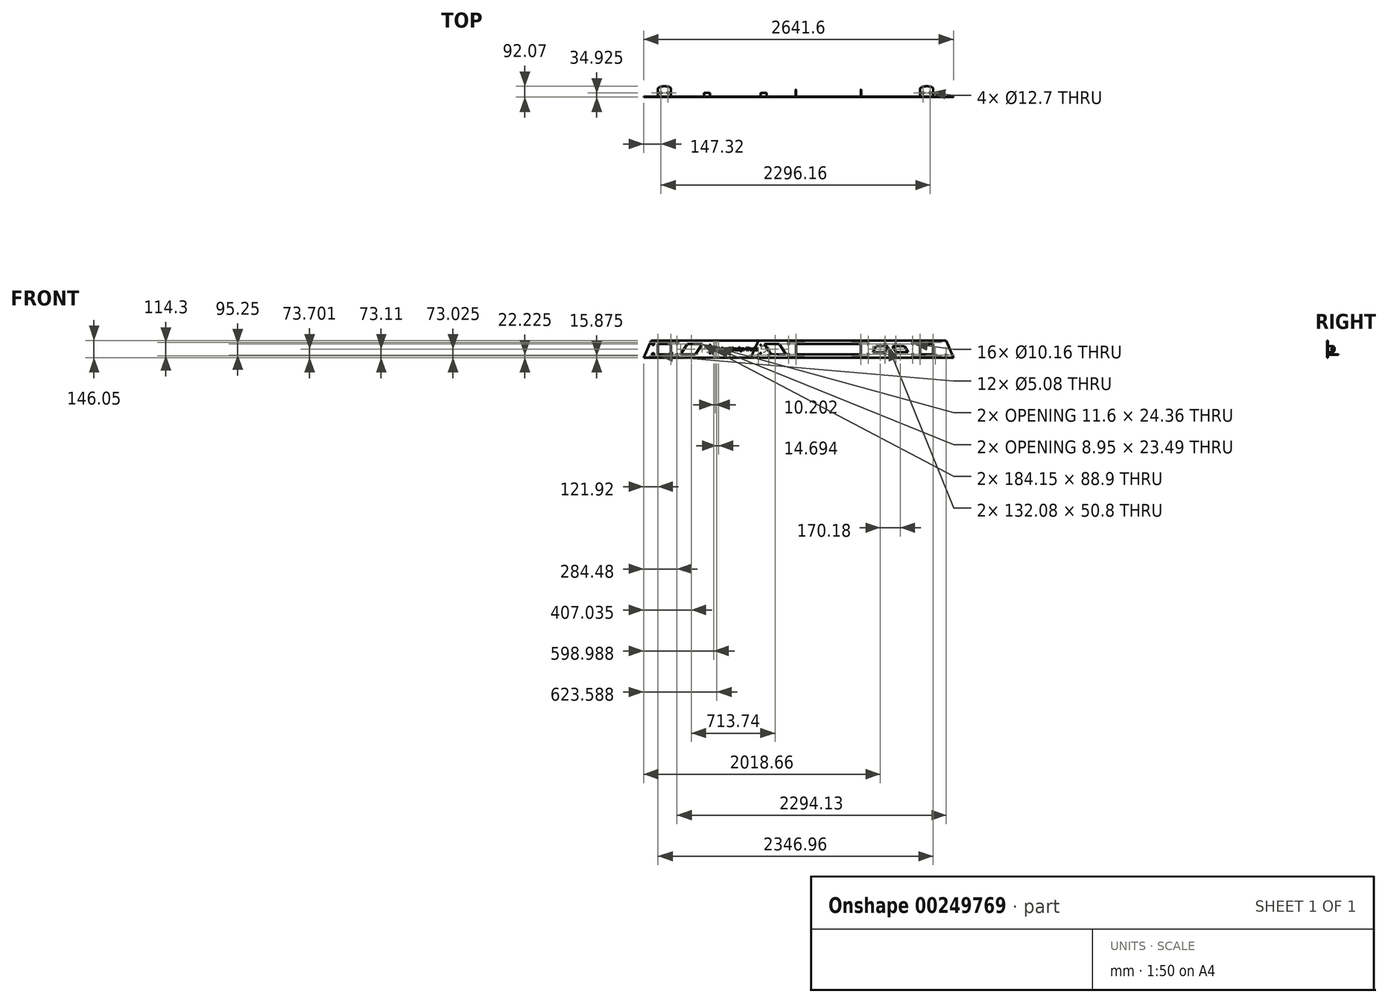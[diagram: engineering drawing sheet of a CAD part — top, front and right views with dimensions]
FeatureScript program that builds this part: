
annotation { "Feature Type Name" : "Feature", "Feature Type Description" : "" }
export const myFeature = defineFeature(function(context is Context, id is Id, definition is map)
    precondition{}
    {
        {
            var Q0;
            Q0=qCreatedBy(makeId("Front.planeOp"),FACE);
            var sketch = newSketch(context, id + "F0", { "sketchPlane" : qUnion([Q0])});
            skLineSegment(sketch, "E0", {"start": v(0, 0) * mm, "end": v(-863.6, 0) * mm});
            skLineSegment(sketch, "E1", {"start": v(-863.6, 0) * mm, "end": v(-800.1, 146.05) * mm});
            skLineSegment(sketch, "E2", {"start": v(-800.1, 146.05) * mm, "end": v(59.06, 146.05) * mm});
            skLineSegment(sketch, "E3", {"start": v(0, 0) * mm, "end": v(0, 425.14) * mm, "construction": true});
            skLineSegment(sketch, "E4.MirrorCS", {"start": v(800.1, 146.05) * mm, "end": v(-59.06, 146.05) * mm});
            skLineSegment(sketch, "E5.MirrorCS", {"start": v(863.6, 0) * mm, "end": v(800.1, 146.05) * mm});
            skLineSegment(sketch, "E6.MirrorCS", {"start": v(0, 0) * mm, "end": v(863.6, 0) * mm});
            skSolve(sketch);
        }
        {
            var Q0;
            Q0 = qSketchRegion(id + "F0", true);
            extrude(context, id + "F1", {"entities" : qUnion([Q0]), "oppositeDirection" : true, "depth" : 3.17 * mm});
        }
        {
            var Q0;
            Q0=makeQuery(id+"F1.opExtrude","CAP_FACE",FACE,{"disambiguationData":[OSD([sQuery(id+"F0.wireOp",EDGE,"E0"),sQuery(id+"F0.wireOp",EDGE,"E1"),sQuery(id+"F0.wireOp",EDGE,"E2"),sQuery(id+"F0.wireOp",EDGE,"E4.MirrorCS"),sQuery(id+"F0.wireOp",EDGE,"E5.MirrorCS"),sQuery(id+"F0.wireOp",EDGE,"E6.MirrorCS")])],"isStart":true});
            var sketch = newSketch(context, id + "F2", { "sketchPlane" : qUnion([Q0])});
            skLineSegment(sketch, "E7.0", {"start": v(-863.6, 0) * mm, "end": v(-800.1, 146.05) * mm});
            skLineSegment(sketch, "E8", {"start": v(-800.1, 146.05) * mm, "end": v(-1714.5, 146.05) * mm});
            skLineSegment(sketch, "E9", {"start": v(-1714.5, 146.05) * mm, "end": v(-1778, 0) * mm});
            skLineSegment(sketch, "E10", {"start": v(-1778, 0) * mm, "end": v(-863.6, 0) * mm});
            skSolve(sketch);
        }
        {
            var Q0;
            Q0 = qSketchRegion(id + "F2", true);
            var Q1;
            Q1=makeQuery(id+"F1.opExtrude","CAP_FACE",FACE,{"disambiguationData":[OSD([sQuery(id+"F0.wireOp",EDGE,"E0"),sQuery(id+"F0.wireOp",EDGE,"E1"),sQuery(id+"F0.wireOp",EDGE,"E2"),sQuery(id+"F0.wireOp",EDGE,"E4.MirrorCS"),sQuery(id+"F0.wireOp",EDGE,"E5.MirrorCS"),sQuery(id+"F0.wireOp",EDGE,"E6.MirrorCS")])],"isStart":false});
            extrude(context, id + "F3", {"entities" : qUnion([Q0]), "endBound" : BoundingType.UP_TO_SURFACE, "oppositeDirection" : true, "endBoundEntityFace" : qUnion([Q1]), "depth" : 25.4 * mm});
        }
        {
            var Q0;
            Q0=makeQuery(id+"F1.opExtrude","CAP_FACE",FACE,{"disambiguationData":[OSD([sQuery(id+"F0.wireOp",EDGE,"E0"),sQuery(id+"F0.wireOp",EDGE,"E1"),sQuery(id+"F0.wireOp",EDGE,"E2"),sQuery(id+"F0.wireOp",EDGE,"E4.MirrorCS"),sQuery(id+"F0.wireOp",EDGE,"E5.MirrorCS"),sQuery(id+"F0.wireOp",EDGE,"E6.MirrorCS")])],"isStart":false});
            var sketch = newSketch(context, id + "F4", { "sketchPlane" : qUnion([Q0])});
            skLineSegment(sketch, "E11", {"start": v(-831.85, 73.02) * mm, "end": v(1871.27, 73.02) * mm, "construction": true});
            skCircle(sketch, "E12", {"center": v(1236.69, 73.02) * mm, "radius": 25.4 * mm});
            skCircle(sketch, "E13", {"center": v(754.09, 73.02) * mm, "radius": 25.4 * mm});
            skSolve(sketch);
        }
        {
            var Q0;
            Q0 = qSketchRegion(id + "F4", true);
            extrude(context, id + "F5", {"entities" : qUnion([Q0]), "operationType" : NewBodyOperationType.ADD, "depth" : 31.75 * mm});
        }
        {
            var Q0;
            Q0=makeQuery(id+"F1.opExtrude","CAP_FACE",FACE,{"disambiguationData":[OSD([sQuery(id+"F0.wireOp",EDGE,"E0"),sQuery(id+"F0.wireOp",EDGE,"E1"),sQuery(id+"F0.wireOp",EDGE,"E2"),sQuery(id+"F0.wireOp",EDGE,"E4.MirrorCS"),sQuery(id+"F0.wireOp",EDGE,"E5.MirrorCS"),sQuery(id+"F0.wireOp",EDGE,"E6.MirrorCS")])],"isStart":true});
            var sketch = newSketch(context, id + "F6", { "sketchPlane" : qUnion([Q0])});
            skLineSegment(sketch, "E14", {"start": v(800.1, 146.05) * mm, "end": v(-1714.5, 146.05) * mm, "construction": true});
            skLineSegment(sketch, "E15", {"start": v(-457.2, 146.05) * mm, "end": v(-457.2, 926.93) * mm, "construction": true});
            skPoint(sketch, "E15.endSnap0", {"position": v(-457.2, 146.05) * mm});
            skLineSegment(sketch, "E16", {"start": v(831.85, 73.02) * mm, "end": v(-1878.84, 73.02) * mm, "construction": true});
            skLineSegment(sketch, "E17.bottom", {"start": v(-478.8, 28.58) * mm, "end": v(72.39, 28.58) * mm});
            skLineSegment(sketch, "E17.top", {"start": v(-478.8, 117.48) * mm, "end": v(72.39, 117.48) * mm});
            skLineSegment(sketch, "E17.left", {"start": v(-478.8, 28.58) * mm, "end": v(-478.8, 117.48) * mm});
            skLineSegment(sketch, "E17.right", {"start": v(72.39, 28.58) * mm, "end": v(72.39, 117.48) * mm});
            skPoint(sketch, "E17.middle", {"position": v(-203.2, 73.02) * mm});
            skLineSegment(sketch, "E18.bottom", {"start": v(690.88, 28.58) * mm, "end": v(579.12, 28.58) * mm});
            skLineSegment(sketch, "E18.top", {"start": v(690.88, 117.48) * mm, "end": v(579.12, 117.47) * mm});
            skLineSegment(sketch, "E18.left", {"start": v(690.88, 28.58) * mm, "end": v(690.88, 117.48) * mm});
            skLineSegment(sketch, "E18.right", {"start": v(579.12, 28.58) * mm, "end": v(579.12, 117.47) * mm});
            skPoint(sketch, "E18.middle", {"position": v(635, 73.03) * mm});
            skCircle(sketch, "E19", {"center": v(135.89, 117.48) * mm, "radius": 5.08 * mm});
            skCircle(sketch, "E20", {"center": v(135.89, 28.58) * mm, "radius": 5.08 * mm});
            skCircle(sketch, "E21", {"center": v(515.62, 28.58) * mm, "radius": 5.08 * mm});
            skCircle(sketch, "E22", {"center": v(515.62, 117.47) * mm, "radius": 5.08 * mm});
            skCircle(sketch, "E23", {"center": v(-542.3, 117.48) * mm, "radius": 5.08 * mm});
            skCircle(sketch, "E24", {"center": v(-542.3, 28.58) * mm, "radius": 5.08 * mm});
            skCircle(sketch, "E25", {"center": v(-478.8, 130.18) * mm, "radius": 2.54 * mm});
            skCircle(sketch, "E26", {"center": v(72.39, 130.18) * mm, "radius": 2.54 * mm});
            skCircle(sketch, "E27.MirrorC", {"center": v(-478.8, 15.87) * mm, "radius": 2.54 * mm});
            skCircle(sketch, "E28.MirrorC", {"center": v(72.39, 15.87) * mm, "radius": 2.54 * mm});
            skCircle(sketch, "E29", {"center": v(579.12, 130.17) * mm, "radius": 2.54 * mm});
            skCircle(sketch, "E30", {"center": v(690.88, 130.18) * mm, "radius": 2.54 * mm});
            skCircle(sketch, "E31.MirrorC", {"center": v(579.12, 15.88) * mm, "radius": 2.54 * mm});
            skCircle(sketch, "E32.MirrorC", {"center": v(690.88, 15.88) * mm, "radius": 2.54 * mm});
            skLineSegment(sketch, "E33.bottom", {"start": v(-1544.32, 28.57) * mm, "end": v(-1656.08, 28.57) * mm});
            skLineSegment(sketch, "E33.top", {"start": v(-1544.32, 117.47) * mm, "end": v(-1656.08, 117.47) * mm});
            skLineSegment(sketch, "E33.left", {"start": v(-1544.32, 28.57) * mm, "end": v(-1544.32, 117.47) * mm});
            skLineSegment(sketch, "E33.right", {"start": v(-1656.08, 28.57) * mm, "end": v(-1656.08, 117.47) * mm});
            skPoint(sketch, "E33.middle", {"position": v(-1600.2, 73.02) * mm});
            skCircle(sketch, "E34", {"center": v(-1493.52, 117.47) * mm, "radius": 5.08 * mm});
            skCircle(sketch, "E35", {"center": v(-1493.52, 28.57) * mm, "radius": 5.08 * mm});
            skCircle(sketch, "E36", {"center": v(-1696.72, 117.47) * mm, "radius": 9.53 * mm});
            skCircle(sketch, "E37", {"center": v(-1696.72, 28.57) * mm, "radius": 9.53 * mm});
            skCircle(sketch, "E38", {"center": v(-1656.08, 130.17) * mm, "radius": 2.54 * mm});
            skCircle(sketch, "E39", {"center": v(-1544.32, 130.17) * mm, "radius": 2.54 * mm});
            skCircle(sketch, "E40.MirrorC", {"center": v(-1656.08, 15.87) * mm, "radius": 2.54 * mm});
            skCircle(sketch, "E41.MirrorC", {"center": v(-1544.32, 15.87) * mm, "radius": 2.54 * mm});
            skLineSegment(sketch, "E42", {"start": v(135.89, 117.47) * mm, "end": v(515.62, 117.48) * mm, "construction": true});
            skLineSegment(sketch, "E43", {"start": v(325.75, 117.48) * mm, "end": v(325.75, 228.13) * mm, "construction": true});
            skCircle(sketch, "E44", {"center": v(371.1, 117.48) * mm, "radius": 5.08 * mm});
            skCircle(sketch, "E45.MirrorC", {"center": v(280.42, 117.48) * mm, "radius": 5.08 * mm});
            skCircle(sketch, "E46.MirrorC", {"center": v(280.42, 28.57) * mm, "radius": 5.08 * mm});
            skCircle(sketch, "E47.MirrorC", {"center": v(371.1, 28.57) * mm, "radius": 5.08 * mm});
            skLineSegment(sketch, "E48", {"start": v(344.8, 98.42) * mm, "end": v(446.4, 98.42) * mm});
            skLineSegment(sketch, "E49", {"start": v(446.4, 98.43) * mm, "end": v(476.88, 47.62) * mm});
            skLineSegment(sketch, "E50", {"start": v(476.88, 47.62) * mm, "end": v(375.28, 47.62) * mm});
            skLineSegment(sketch, "E51", {"start": v(375.28, 47.62) * mm, "end": v(344.8, 98.42) * mm});
            skLineSegment(sketch, "E52.MirrorCS", {"start": v(306.7, 98.42) * mm, "end": v(205.1, 98.42) * mm});
            skLineSegment(sketch, "E53.MirrorCS", {"start": v(276.22, 47.62) * mm, "end": v(306.7, 98.42) * mm});
            skLineSegment(sketch, "E54.MirrorCS", {"start": v(174.62, 47.62) * mm, "end": v(276.22, 47.62) * mm});
            skLineSegment(sketch, "E55.MirrorCS", {"start": v(205.1, 98.43) * mm, "end": v(174.62, 47.62) * mm});
            skLineSegment(sketch, "E56", {"start": v(-1278.9, 117.47) * mm, "end": v(-1405.9, 117.47) * mm});
            skLineSegment(sketch, "E57", {"start": v(-1405.9, 117.47) * mm, "end": v(-1463.04, 28.57) * mm});
            skLineSegment(sketch, "E58", {"start": v(-1463.04, 28.57) * mm, "end": v(-1336.04, 28.57) * mm});
            skLineSegment(sketch, "E59", {"start": v(-1336.04, 28.57) * mm, "end": v(-1278.9, 117.47) * mm});
            skCircle(sketch, "E60", {"center": v(-779.49, 107.95) * mm, "radius": 3.18 * mm});
            skCircle(sketch, "E61", {"center": v(-1211.29, 107.95) * mm, "radius": 3.17 * mm});
            skCircle(sketch, "E62.MirrorC", {"center": v(-1211.29, 38.1) * mm, "radius": 3.17 * mm});
            skCircle(sketch, "E63.MirrorC", {"center": v(-779.49, 38.1) * mm, "radius": 3.18 * mm});
            skLineSegment(sketch, "E64", {"start": v(-622.3, 117.48) * mm, "end": v(-749.3, 117.48) * mm});
            skLineSegment(sketch, "E65", {"start": v(-749.3, 117.48) * mm, "end": v(-692.15, 28.58) * mm});
            skLineSegment(sketch, "E66", {"start": v(-692.15, 28.58) * mm, "end": v(-565.15, 28.58) * mm});
            skLineSegment(sketch, "E67", {"start": v(-565.15, 28.58) * mm, "end": v(-622.3, 117.48) * mm});
            skSolve(sketch);
        }
        {
            var Q0;
            Q0 = qSketchRegion(id + "F6", true);
            extrude(context, id + "F7", {"entities" : qUnion([Q0]), "operationType" : NewBodyOperationType.REMOVE, "oppositeDirection" : true, "depth" : 25.4 * mm});
        }
        {
            var Q0;
            Q0=makeQuery(id+"F1.opExtrude","CAP_FACE",FACE,{"disambiguationData":[OSD([sQuery(id+"F0.wireOp",EDGE,"E0"),sQuery(id+"F0.wireOp",EDGE,"E1"),sQuery(id+"F0.wireOp",EDGE,"E2"),sQuery(id+"F0.wireOp",EDGE,"E4.MirrorCS"),sQuery(id+"F0.wireOp",EDGE,"E5.MirrorCS"),sQuery(id+"F0.wireOp",EDGE,"E6.MirrorCS")])],"isStart":true});
            var sketch = newSketch(context, id + "F8", { "sketchPlane" : qUnion([Q0])});
            skCircle(sketch, "E68", {"center": v(800.6, 22.23) * mm, "radius": 5.08 * mm});
            skCircle(sketch, "E69", {"center": v(709.93, 22.23) * mm, "radius": 5.08 * mm});
            skLineSegment(sketch, "E70", {"start": v(0, 0) * mm, "end": v(0, -220.42) * mm, "construction": true});
            skCircle(sketch, "E71.MirrorC", {"center": v(-709.93, 22.22) * mm, "radius": 5.08 * mm});
            skCircle(sketch, "E72.MirrorC", {"center": v(-800.6, 22.22) * mm, "radius": 5.08 * mm});
            skSolve(sketch);
        }
        {
            var Q0;
            Q0 = qSketchRegion(id + "F8", true);
            var Q1;
            Q1=makeQuery(id+"F1.opExtrude","CAP_FACE",FACE,{"disambiguationData":[OSD([sQuery(id+"F0.wireOp",EDGE,"E0"),sQuery(id+"F0.wireOp",EDGE,"E1"),sQuery(id+"F0.wireOp",EDGE,"E2"),sQuery(id+"F0.wireOp",EDGE,"E4.MirrorCS"),sQuery(id+"F0.wireOp",EDGE,"E5.MirrorCS"),sQuery(id+"F0.wireOp",EDGE,"E6.MirrorCS")])],"isStart":false});
            extrude(context, id + "F9", {"entities" : qUnion([Q0]), "operationType" : NewBodyOperationType.REMOVE, "endBound" : BoundingType.UP_TO_SURFACE, "oppositeDirection" : true, "endBoundEntityFace" : qUnion([Q1]), "depth" : 25.4 * mm});
        }
        {
            var Q0;
            Q0=makeQuery(id+"F7.boolean.opBoolean","COPY",FACE,{"derivedFrom":makeQuery(id+"F7.opExtrude","SWEPT_FACE",FACE,{"disambiguationData":[OSD([sQuery(id+"F6.wireOp",EDGE,"E33.bottom")])]})});
            var sketch = newSketch(context, id + "F10", { "sketchPlane" : qUnion([Q0])});
            skLineSegment(sketch, "E73", {"start": v(-1600.2, 3.18) * mm, "end": v(-1600.2, 59.04) * mm, "construction": true});
            skPoint(sketch, "E73.endSnap0", {"position": v(-1600.2, 3.18) * mm});
            skLineSegment(sketch, "E74", {"start": v(-1656.08, 3.18) * mm, "end": v(-1656.08, 71.76) * mm});
            skLineSegment(sketch, "E75.MirrorCS", {"start": v(-1544.32, 3.18) * mm, "end": v(-1544.32, 71.76) * mm});
            skEllipticalArc(sketch, "E76", {});
            skLineSegment(sketch, "E77", {"start": v(-1656.08, 3.18) * mm, "end": v(-1544.32, 3.18) * mm});
            skCircle(sketch, "E78", {"center": v(-1630.68, 34.93) * mm, "radius": 6.35 * mm});
            skCircle(sketch, "E79.MirrorC", {"center": v(-1569.72, 34.93) * mm, "radius": 6.35 * mm});
            skLineSegment(sketch, "E80", {"start": v(690.88, 3.18) * mm, "end": v(579.12, 3.17) * mm, "construction": true});
            skLineSegment(sketch, "E81", {"start": v(635, 3.18) * mm, "end": v(635, 23.98) * mm, "construction": true});
            skLineSegment(sketch, "E82", {"start": v(579.12, 3.17) * mm, "end": v(579.12, 71.76) * mm});
            skLineSegment(sketch, "E83.MirrorCS", {"start": v(690.88, 3.17) * mm, "end": v(690.88, 71.76) * mm});
            skEllipticalArc(sketch, "E84", {});
            skLineSegment(sketch, "E85", {"start": v(579.12, 3.17) * mm, "end": v(690.88, 3.18) * mm});
            skCircle(sketch, "E86", {"center": v(604.52, 34.93) * mm, "radius": 6.35 * mm});
            skCircle(sketch, "E87.MirrorC", {"center": v(665.48, 34.93) * mm, "radius": 6.35 * mm});
            const initialGuessF10  = {"E76": [-1.6002, 0.071755, -1, 0, 0.05588, 0.02032, 3.141592653589793, 0], "E84": [0.635, 0.071755, -1, 0, 0.05588, 0.02032, 3.141592653589793, 0]};
            skSetInitialGuess(sketch, initialGuessF10);
            skSolve(sketch);
        }
        {
            var Q0;
            Q0 = qSketchRegion(id + "F10", true);
            extrude(context, id + "F11", {"entities" : qUnion([Q0]), "operationType" : NewBodyOperationType.ADD, "oppositeDirection" : true, "depth" : 3.17 * mm});
        }
        {
            var Q0;
            Q0=makeQuery(id+"F3.opExtrude","CAP_FACE",FACE,{"disambiguationData":[OSD([sQuery(id+"F2.wireOp",EDGE,"E7.0"),sQuery(id+"F2.wireOp",EDGE,"E8"),sQuery(id+"F2.wireOp",EDGE,"E9"),sQuery(id+"F2.wireOp",EDGE,"E10")])],"isStart":true});
            var sketch = newSketch(context, id + "F12", { "sketchPlane" : qUnion([Q0])});
            skText(sketch, "E88", { "text": "Off-Road Design Works", "fontName": "AllertaStencil-Regular.ttf"});
            skLineSegment(sketch, "E89", {"start": v(-1185.89, 73.02) * mm, "end": v(-1225.5, 73.02) * mm, "construction": true});
            const initialGuessF12  = {"E88": [-1.18589, 0.06152, 1, 0, 0.023]};
            skSetInitialGuess(sketch, initialGuessF12);
            skSolve(sketch);
        }
        {
            var Q0;
            Q0 = qSketchRegion(id + "F12", true);
            var Q1;
            Q1=makeQuery(id+"F3.opExtrude","CAP_FACE",FACE,{"disambiguationData":[OSD([sQuery(id+"F2.wireOp",EDGE,"E7.0"),sQuery(id+"F2.wireOp",EDGE,"E8"),sQuery(id+"F2.wireOp",EDGE,"E9"),sQuery(id+"F2.wireOp",EDGE,"E10")])],"isStart":false});
            extrude(context, id + "F13", {"entities" : qUnion([Q0]), "operationType" : NewBodyOperationType.REMOVE, "endBound" : BoundingType.UP_TO_SURFACE, "oppositeDirection" : true, "endBoundEntityFace" : qUnion([Q1]), "depth" : 25.4 * mm});
        }
        {
            var Q0;
            Q0=makeQuery(id+"F7.boolean.opBoolean","COPY",FACE,{"derivedFrom":makeQuery(id+"F7.opExtrude","SWEPT_FACE",FACE,{"disambiguationData":[OSD([sQuery(id+"F6.wireOp",EDGE,"E17.right")])]})});
            var sketch = newSketch(context, id + "F14", { "sketchPlane" : qUnion([Q0])});
            skLineSegment(sketch, "E90", {"start": v(-3.18, 73.02) * mm, "end": v(-34, 73.02) * mm, "construction": true});
            skLineSegment(sketch, "E91", {"start": v(-3.18, 98.42) * mm, "end": v(-47.62, 98.42) * mm});
            skLineSegment(sketch, "E92.MirrorCS", {"start": v(-3.18, 47.62) * mm, "end": v(-47.62, 47.62) * mm});
            skEllipticalArc(sketch, "E93", {});
            skCircle(sketch, "E94", {"center": v(-40, 73.02) * mm, "radius": 6.35 * mm});
            skLineSegment(sketch, "E95", {"start": v(-3.18, 98.42) * mm, "end": v(-3.18, 47.62) * mm});
            const initialGuessF14  = {"E93": [-0.047625, 0.073025, 0, 1, 0.0254, 0.01524, 0, 3.141592653589793]};
            skSetInitialGuess(sketch, initialGuessF14);
            skSolve(sketch);
        }
        {
            var Q0;
            Q0 = qSketchRegion(id + "F14", true);
            extrude(context, id + "F15", {"entities" : qUnion([Q0]), "oppositeDirection" : true, "depth" : 3.17 * mm});
        }
        {
            var Q0;
            Q0=makeQuery(id+"F7.boolean.opBoolean","COPY",FACE,{"derivedFrom":makeQuery(id+"F7.opExtrude","SWEPT_FACE",FACE,{"disambiguationData":[OSD([sQuery(id+"F6.wireOp",EDGE,"E17.right")])]})});
            var Q1;
            Q1=makeQuery(id+"F7.boolean.opBoolean","COPY",FACE,{"derivedFrom":makeQuery(id+"F7.opExtrude","SWEPT_FACE",FACE,{"disambiguationData":[OSD([sQuery(id+"F6.wireOp",EDGE,"E17.left")])]})});
            cPlane(context, id + "F16", {"entities" : qUnion([Q0, Q1]), "cplaneType" : CPlaneType.MID_PLANE, "offset" : 25.4 * mm, "width" : 152.4 * mm, "height" : 152.4 * mm});
        }
        {
            var Q0;
            Q0=makeQuery(id+"F15.opExtrude","SWEPT_BODY",BODY,{"disambiguationData":[OSD([sQuery(id+"F14.wireOp",EDGE,"E91"),sQuery(id+"F14.wireOp",EDGE,"E92.MirrorCS"),sQuery(id+"F14.wireOp",EDGE,"E93"),sQuery(id+"F14.wireOp",EDGE,"E94"),sQuery(id+"F14.wireOp",EDGE,"E95")])]});
            var Q1;
            Q1=qCreatedBy(id+"F16.planeOp",FACE);
            mirror(context, id + "F17", {"operationType" : NewBodyOperationType.ADD, "entities" : qUnion([Q0]), "mirrorPlane" : qUnion([Q1])});
        }
    });
